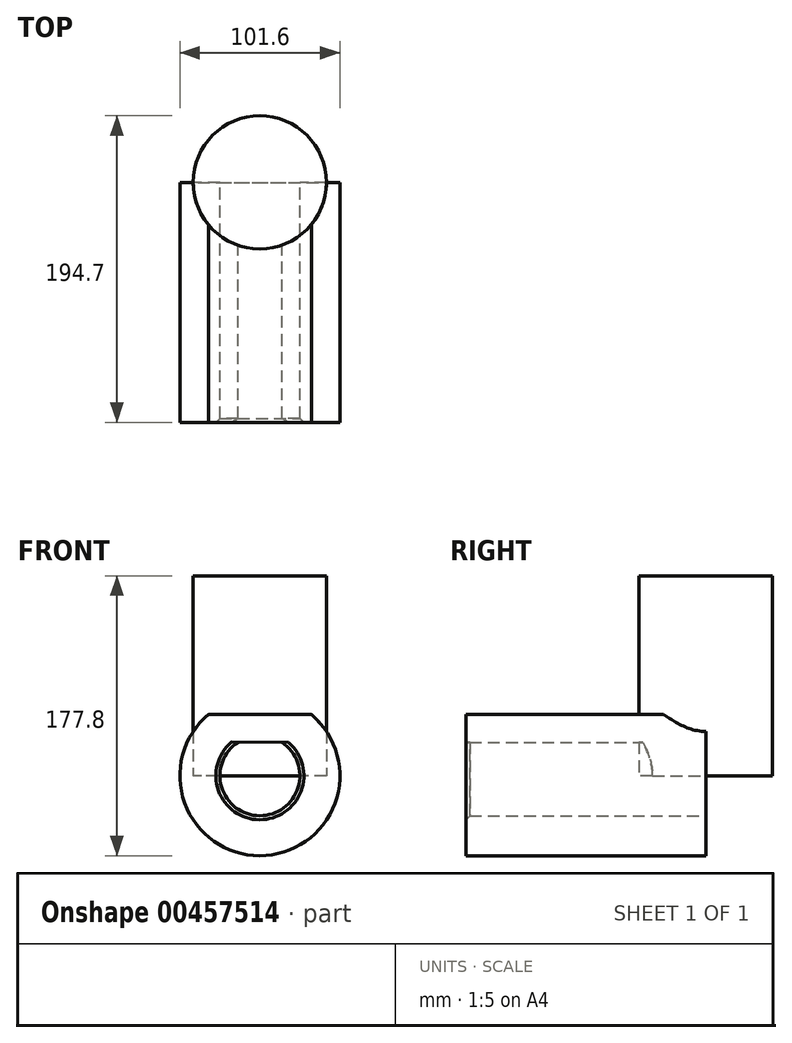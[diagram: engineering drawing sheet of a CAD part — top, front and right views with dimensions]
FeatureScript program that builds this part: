
annotation { "Feature Type Name" : "Feature", "Feature Type Description" : "" }
export const myFeature = defineFeature(function(context is Context, id is Id, definition is map)
    precondition{}
    {
        {
            var Q0;
            Q0=qCreatedBy(makeId("Top.planeOp"),FACE);
            var sketch = newSketch(context, id + "F0", { "sketchPlane" : qUnion([Q0])});
            skCircle(sketch, "E0", {"center": v(0, 0) * mm, "radius": 42.3 * mm});
            skSolve(sketch);
        }
        {
            var Q0;
            Q0=qCreatedBy(makeId("Front.planeOp"),FACE);
            var sketch = newSketch(context, id + "F1", { "sketchPlane" : qUnion([Q0])});
            skArc(sketch, "E1", {"start": v(32.72, 38.86) * mm, "mid": v(-0.1, -50.8) * mm, "end": v(-32.55, 39) * mm});
            skLineSegment(sketch, "E2", {"start": v(-32.55, 39) * mm, "end": v(32.72, 38.86) * mm});
            skArc(sketch, "E3", {"start": v(14.08, 21.14) * mm, "mid": v(-0.16, -25.4) * mm, "end": v(-13.8, 21.32) * mm});
            skLineSegment(sketch, "E4", {"start": v(-13.8, 21.32) * mm, "end": v(14.08, 21.14) * mm});
            skSolve(sketch);
        }
        {
            var Q0;
            Q0 = qSketchRegion(id + "F1", true);
            extrude(context, id + "F2", {"entities" : qUnion([Q0]), "depth" : 25.4 * mm});
        }
        {
            var Q0;
            Q0=makeQuery(id+"F2.opExtrude","CAP_FACE",FACE,{"disambiguationData":[OSD([sQuery(id+"F1.wireOp",EDGE,"E1"),sQuery(id+"F1.wireOp",EDGE,"E2"),sQuery(id+"F1.wireOp",EDGE,"E3"),sQuery(id+"F1.wireOp",EDGE,"E4")])],"isStart":false});
            extrude(context, id + "F3", {"entities" : qUnion([Q0]), "operationType" : NewBodyOperationType.ADD, "depth" : 127 * mm});
        }
        {
            var Q0;
            Q0=makeQuery(id+"F3.opExtrude","CAP_EDGE",EDGE,{"disambiguationData":[OSD([sQuery(id+"F1.wireOp",EDGE,"E3")])],"isStart":false});
            chamfer(context, id + "F4", {"entities" : qUnion([Q0]), "width" : 2.54 * mm, "tangentPropagation" : true});
        }
        {
            var Q0;
            Q0 = qSketchRegion(id + "F0", true);
            extrude(context, id + "F5", {"entities" : qUnion([Q0]), "operationType" : NewBodyOperationType.ADD, "depth" : 127 * mm});
        }
    });
